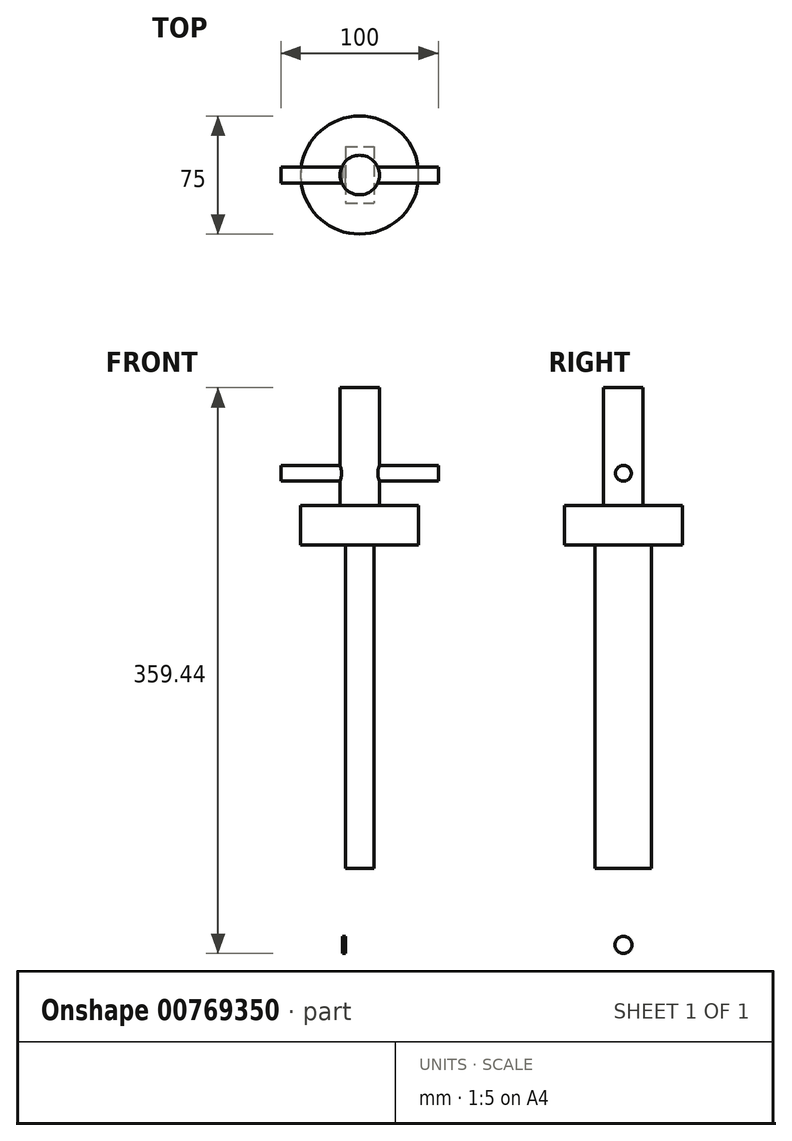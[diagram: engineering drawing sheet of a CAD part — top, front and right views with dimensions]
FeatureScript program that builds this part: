
annotation { "Feature Type Name" : "Feature", "Feature Type Description" : "" }
export const myFeature = defineFeature(function(context is Context, id is Id, definition is map)
    precondition{}
    {
        {
            var Q0;
            Q0=qCreatedBy(makeId("Top.planeOp"),FACE);
            var sketch = newSketch(context, id + "F0", { "sketchPlane" : qUnion([Q0])});
            skCircle(sketch, "E0", {"center": v(0, 0) * mm, "radius": 37.5 * mm});
            skSolve(sketch);
        }
        {
            var Q0;
            Q0=makeQuery(id+"F0.imprint","IMPRINT",FACE,{"disambiguationData":[TD([[makeQuery(id+"F0.imprint","IMPRINT",EDGE,{"derivedFrom":sQuery(id+"F0.wireOp",EDGE,"E0")}),1.0]])]});
            extrude(context, id + "F1", {"entities" : qUnion([Q0]), "depth" : 25 * mm, "offsetDistance" : 25 * mm});
        }
        {
            var Q0;
            Q0=makeQuery(id+"F1.opExtrude","CAP_FACE",FACE,{"disambiguationData":[OSD([sQuery(id+"F0.wireOp",EDGE,"E0")])],"isStart":true});
            var sketch = newSketch(context, id + "F2", { "sketchPlane" : qUnion([Q0])});
            skLineSegment(sketch, "E1.bottom", {"start": v(-9.02, -17.95) * mm, "end": v(9.02, -17.95) * mm});
            skLineSegment(sketch, "E1.top", {"start": v(-9.02, 17.95) * mm, "end": v(9.02, 17.95) * mm});
            skLineSegment(sketch, "E1.left", {"start": v(-9.02, -17.95) * mm, "end": v(-9.02, 17.95) * mm});
            skLineSegment(sketch, "E1.right", {"start": v(9.02, -17.95) * mm, "end": v(9.02, 17.95) * mm});
            skPoint(sketch, "E1.middle", {"position": v(0, 0) * mm});
            skSolve(sketch);
        }
        {
            var Q0;
            Q0 = qSketchRegion(id + "F2", true);
            extrude(context, id + "F3", {"entities" : qUnion([Q0]), "operationType" : NewBodyOperationType.ADD, "depth" : 205.5 * mm, "offsetDistance" : 25 * mm});
        }
        {
            var Q0;
            Q0=makeQuery(id+"F3.opExtrude","SWEPT_FACE",FACE,{"disambiguationData":[OSD([sQuery(id+"F2.wireOp",EDGE,"E1.left")])]});
            var sketch = newSketch(context, id + "F4", { "sketchPlane" : qUnion([Q0])});
            skCircle(sketch, "E2", {"center": v(0, -254) * mm, "radius": 5.44 * mm});
            skPoint(sketch, "E2.centerSnap0", {"position": v(0, -205.5) * mm});
            skSolve(sketch);
        }
        {
            var Q0;
            Q0 = qSketchRegion(id + "F4", true);
            extrude(context, id + "F5", {"entities" : qUnion([Q0]), "operationType" : NewBodyOperationType.ADD, "depth" : 2 * mm, "offsetDistance" : 25 * mm});
        }
        {
            var Q0;
            Q0=makeQuery(id+"F1.opExtrude","CAP_FACE",FACE,{"disambiguationData":[OSD([sQuery(id+"F0.wireOp",EDGE,"E0")])],"isStart":false});
            var sketch = newSketch(context, id + "F6", { "sketchPlane" : qUnion([Q0])});
            skCircle(sketch, "E3", {"center": v(0, 0) * mm, "radius": 12.54 * mm});
            skSolve(sketch);
        }
        {
            var Q0;
            Q0=makeQuery(id+"F6.imprint","IMPRINT",FACE,{"disambiguationData":[TD([[makeQuery(id+"F6.imprint","IMPRINT",EDGE,{"derivedFrom":sQuery(id+"F6.wireOp",EDGE,"E3")}),1.0]])]});
            extrude(context, id + "F7", {"entities" : qUnion([Q0]), "operationType" : NewBodyOperationType.ADD, "depth" : 75 * mm, "offsetDistance" : 25 * mm});
        }
        {
            var Q0;
            Q0=qCreatedBy(makeId("Right.planeOp"),FACE);
            var sketch = newSketch(context, id + "F8", { "sketchPlane" : qUnion([Q0])});
            skCircle(sketch, "E4", {"center": v(0, 45.58) * mm, "radius": 5 * mm});
            skSolve(sketch);
        }
        {
            var Q0;
            Q0 = qSketchRegion(id + "F8", true);
            extrude(context, id + "F9", {"entities" : qUnion([Q0]), "operationType" : NewBodyOperationType.ADD, "depth" : 50 * mm, "offsetDistance" : 25 * mm});
        }
        {
            var Q0;
            Q0 = qSketchRegion(id + "F8", true);
            extrude(context, id + "F10", {"entities" : qUnion([Q0]), "operationType" : NewBodyOperationType.ADD, "oppositeDirection" : true, "depth" : 50 * mm, "offsetDistance" : 25 * mm});
        }
    });
